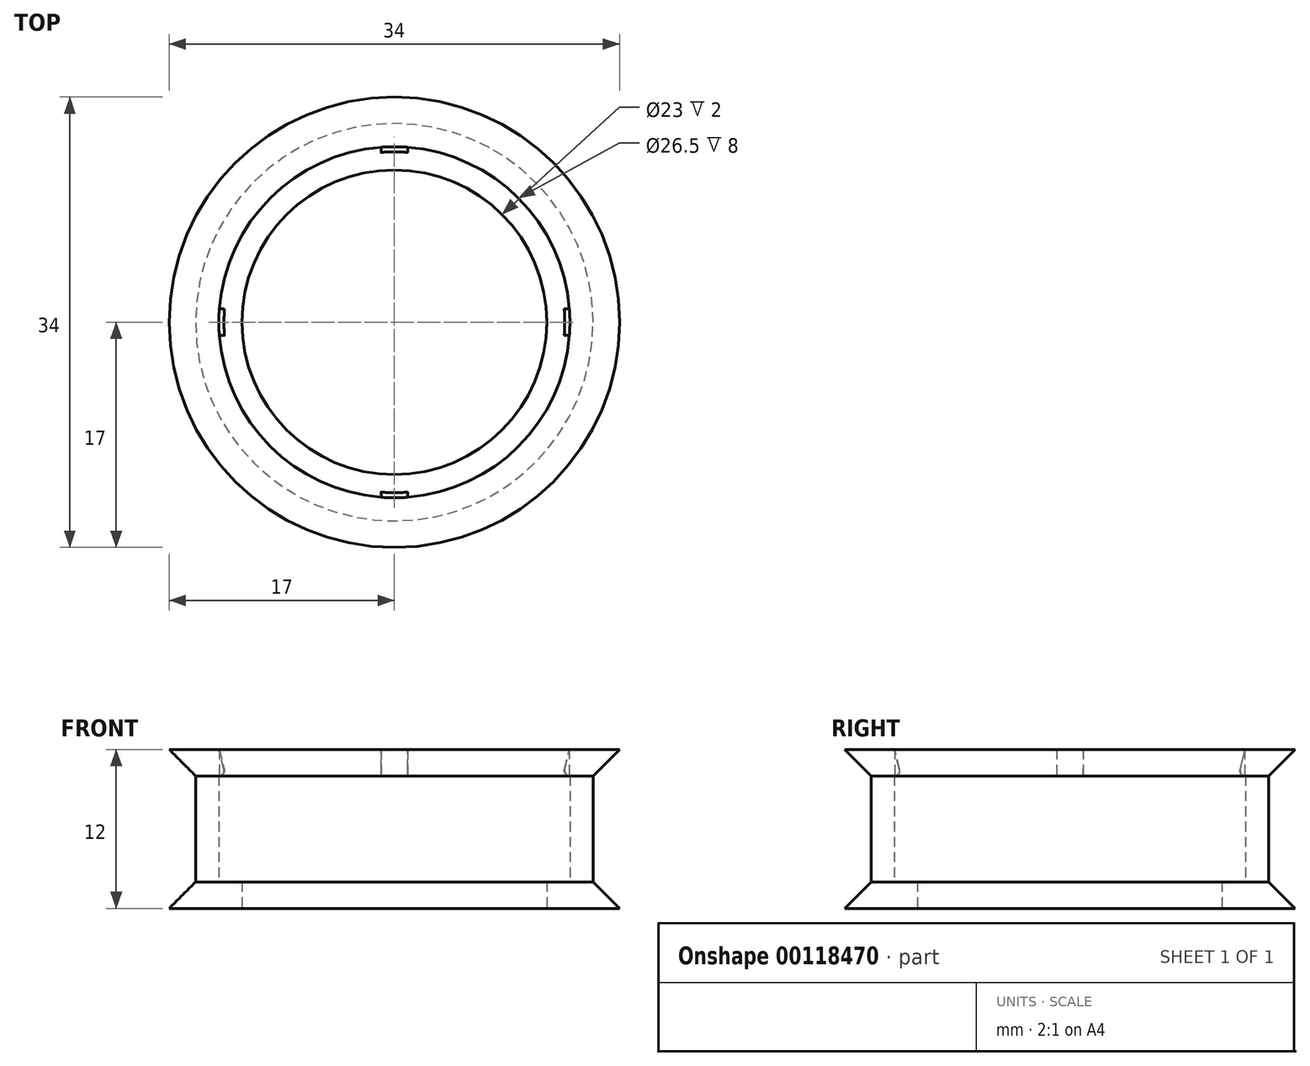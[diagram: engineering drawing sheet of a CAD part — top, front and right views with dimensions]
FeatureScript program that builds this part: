
annotation { "Feature Type Name" : "Feature", "Feature Type Description" : "" }
export const myFeature = defineFeature(function(context is Context, id is Id, definition is map)
    precondition{}
    {
        {
            var Q0;
            Q0=qCreatedBy(makeId("Right.planeOp"),FACE);
            var sketch = newSketch(context, id + "F0", { "sketchPlane" : qUnion([Q0])});
            skLineSegment(sketch, "E0", {"start": v(-11.5, 0) * mm, "end": v(-11.5, 2) * mm});
            skLineSegment(sketch, "E1", {"start": v(-11.5, 2) * mm, "end": v(-13.25, 2) * mm});
            skLineSegment(sketch, "E2", {"start": v(-13.25, 2) * mm, "end": v(-13.25, 10) * mm});
            skLineSegment(sketch, "E3", {"start": v(-13.26, 10) * mm, "end": v(-13.25, 10) * mm});
            skLineSegment(sketch, "E4", {"start": v(-12.75, 10) * mm, "end": v(-12.75, 10) * mm});
            skLineSegment(sketch, "E5", {"start": v(-13.25, 12) * mm, "end": v(-17, 12) * mm});
            skLineSegment(sketch, "E6", {"start": v(-17, 12) * mm, "end": v(-15, 10) * mm});
            skLineSegment(sketch, "E7", {"start": v(-15, 10) * mm, "end": v(-15, 2) * mm});
            skLineSegment(sketch, "E8", {"start": v(-15, 2) * mm, "end": v(-17, 0) * mm});
            skLineSegment(sketch, "E9", {"start": v(-17, 0) * mm, "end": v(-11.5, 0) * mm});
            skLineSegment(sketch, "E10.MirrorCS", {"start": v(13.25, 2) * mm, "end": v(13.25, 10) * mm});
            skLineSegment(sketch, "E11.MirrorCS", {"start": v(13.26, 10) * mm, "end": v(13.25, 10) * mm});
            skLineSegment(sketch, "E12.MirrorCS", {"start": v(12.87, 10.5) * mm, "end": v(13.25, 12) * mm});
            skLineSegment(sketch, "E13.MirrorCS", {"start": v(13.25, 12) * mm, "end": v(17, 12) * mm});
            skLineSegment(sketch, "E14.MirrorCS", {"start": v(17, 12) * mm, "end": v(15, 10) * mm});
            skLineSegment(sketch, "E15.MirrorCS", {"start": v(15, 10) * mm, "end": v(15, 2) * mm});
            skLineSegment(sketch, "E16.MirrorCS", {"start": v(15, 2) * mm, "end": v(17, 0) * mm});
            skLineSegment(sketch, "E17.MirrorCS", {"start": v(17, 0) * mm, "end": v(11.5, 0) * mm});
            skLineSegment(sketch, "E18.MirrorCS", {"start": v(11.5, 0) * mm, "end": v(11.5, 2) * mm});
            skLineSegment(sketch, "E19.MirrorCS", {"start": v(11.5, 2) * mm, "end": v(13.25, 2) * mm});
            skLineSegment(sketch, "E20", {"start": v(-15, 6) * mm, "end": v(-13.25, 6) * mm, "construction": true});
            skLineSegment(sketch, "E21", {"start": v(0, 0) * mm, "end": v(0, 12) * mm, "construction": true});
            skPoint(sketch, "E22.visualSharp", {"position": v(12.75, 10) * mm});
            skArc(sketch, "E22.filletArc", {"start": v(12.87, 10.5) * mm, "mid": v(12.95, 10.15) * mm, "end": v(13.26, 10) * mm});
            skLineSegment(sketch, "E23", {"start": v(-12.87, 10.5) * mm, "end": v(-13.25, 12) * mm});
            skPoint(sketch, "E24.visualSharp", {"position": v(-12.75, 10) * mm});
            skArc(sketch, "E24.filletArc", {"start": v(-13.26, 10) * mm, "mid": v(-12.95, 10.15) * mm, "end": v(-12.87, 10.5) * mm});
            skSolve(sketch);
        }
        {
            var Q0;
            Q0=makeQuery(id+"F0.imprint","IMPRINT",FACE,{"disambiguationData":[TD([[makeQuery(id+"F0.imprint","IMPRINT",EDGE,{"derivedFrom":sQuery(id+"F0.wireOp",EDGE,"E0")}),1.0]])]});
            var Q1;
            Q1=sQuery(id+"F0.wireOp",EDGE,"E21");
            revolve(context, id + "F1", {"entities" : qUnion([Q0]), "axis" : qUnion([Q1]), "revolveType" : RevolveType.FULL});
        }
        {
            var Q0;
            Q0=qCreatedBy(makeId("Top.planeOp"),FACE);
            var sketch = newSketch(context, id + "F2", { "sketchPlane" : qUnion([Q0])});
            skLineSegment(sketch, "E25", {"start": v(-13.21, 1) * mm, "end": v(-1, 1) * mm});
            skLineSegment(sketch, "E26", {"start": v(-1, 13.21) * mm, "end": v(-1, 1) * mm});
            skLineSegment(sketch, "E27.MirrorCS", {"start": v(1, 13.21) * mm, "end": v(1, 1) * mm});
            skLineSegment(sketch, "E28.MirrorCS", {"start": v(-13.21, -1) * mm, "end": v(-1, -1) * mm});
            skArc(sketch, "E29", {"start": v(-1, 13.21) * mm, "mid": v(-9.37, 9.37) * mm, "end": v(-13.21, 1) * mm});
            skArc(sketch, "E30", {"start": v(-13.21, 1) * mm, "mid": v(-13.25, 0) * mm, "end": v(-13.21, -1) * mm, "construction": true});
            skArc(sketch, "E31", {"start": v(-13.21, -1) * mm, "mid": v(-9.37, -9.37) * mm, "end": v(-1, -13.21) * mm});
            skArc(sketch, "E32", {"start": v(-1, -13.21) * mm, "mid": v(0, -13.25) * mm, "end": v(1, -13.21) * mm, "construction": true});
            skArc(sketch, "E33", {"start": v(1, -13.21) * mm, "mid": v(9.37, -9.37) * mm, "end": v(13.21, -1) * mm});
            skArc(sketch, "E34", {"start": v(13.21, -1) * mm, "mid": v(13.25, 0) * mm, "end": v(13.21, 1) * mm, "construction": true});
            skArc(sketch, "E35", {"start": v(13.21, 1) * mm, "mid": v(9.37, 9.37) * mm, "end": v(1, 13.21) * mm});
            skArc(sketch, "E36", {"start": v(1, 13.21) * mm, "mid": v(0, 13.25) * mm, "end": v(-1, 13.21) * mm, "construction": true});
            skLineSegment(sketch, "E37", {"start": v(-1, 1) * mm, "end": v(1, 1) * mm, "construction": true});
            skLineSegment(sketch, "E38", {"start": v(1, 1) * mm, "end": v(13.21, 1) * mm});
            skLineSegment(sketch, "E39", {"start": v(1, -1) * mm, "end": v(13.21, -1) * mm});
            skLineSegment(sketch, "E40", {"start": v(-1, -1) * mm, "end": v(1, -1) * mm, "construction": true});
            skLineSegment(sketch, "E41", {"start": v(-1, -1) * mm, "end": v(-1, -13.21) * mm});
            skLineSegment(sketch, "E42", {"start": v(-1, 1) * mm, "end": v(-1, -1) * mm, "construction": true});
            skLineSegment(sketch, "E43", {"start": v(1, 1) * mm, "end": v(1, -1) * mm, "construction": true});
            skLineSegment(sketch, "E44", {"start": v(1, -1) * mm, "end": v(1, -13.21) * mm});
            skSolve(sketch);
        }
        {
            var Q0;
            Q0=makeQuery(id+"F2.imprint","IMPRINT",FACE,{"disambiguationData":[TD([[makeQuery(id+"F2.imprint","IMPRINT",EDGE,{"derivedFrom":sQuery(id+"F2.wireOp",EDGE,"E25")}),1.0]])]});
            var Q1;
            Q1=makeQuery(id+"F2.imprint","IMPRINT",FACE,{"disambiguationData":[TD([[makeQuery(id+"F2.imprint","IMPRINT",EDGE,{"derivedFrom":sQuery(id+"F2.wireOp",EDGE,"E27.MirrorCS")}),1.0]])]});
            var Q2;
            Q2=makeQuery(id+"F2.imprint","IMPRINT",FACE,{"disambiguationData":[TD([[makeQuery(id+"F2.imprint","IMPRINT",EDGE,{"derivedFrom":sQuery(id+"F2.wireOp",EDGE,"E33")}),1.0]])]});
            var Q3;
            Q3=makeQuery(id+"F2.imprint","IMPRINT",FACE,{"disambiguationData":[TD([[makeQuery(id+"F2.imprint","IMPRINT",EDGE,{"derivedFrom":sQuery(id+"F2.wireOp",EDGE,"E28.MirrorCS")}),-1.0]])]});
            var Q4;
            Q4=makeQuery(id+"F1.opRevolve","SWEPT_FACE",FACE,{"disambiguationData":[OSD([sQuery(id+"F0.wireOp",EDGE,"E1")])]});
            extrude(context, id + "F3", {"entities" : qUnion([Q0, Q1, Q2, Q3]), "operationType" : NewBodyOperationType.REMOVE, "endBound" : BoundingType.THROUGH_ALL, "depth" : 25 * mm, "hasSecondDirection" : true, "secondDirectionBound" : SecondDirectionBoundingType.UP_TO_SURFACE, "secondDirectionOppositeDirection" : false, "secondDirectionBoundEntityFace" : qUnion([Q4]), "secondDirectionDepth" : 25 * mm});
        }
    });
